# Revit family: CADS_AIRFLOWdev_AirflexPro_Round_DistributionBox_6PortNarrow
name_source: partatom
category: Duct Accessories
units: mm (PartAtom-declared; Revit-internal decimal feet)

## family parameters
Always vertical = Yes
Cut with Voids When Loaded = No
OmniClass Number = 23.75.00.00
OmniClass Title = Climate Control (HVAC)
Part Type = Breaks Into
Round Connector Dimension = Use Diameter
Shared = No
Work Plane-Based = No

## types (1)
- CADS_AIRFLOWdev_AirflexPro_Round_DistributionBox_6PortNarrow
    6MonthlyMaintenance = Visually inspect system, clean the fan and ducting if necessary
    AirflowRateRange = 54.0 L/s
    AssemblyPlace = UNKNOWN
    AssetType = FIXED
    Body = CADS_AIRFLOWdev_SteelGalvanized
    CADS_Index = 0
    CEApproval = Yes
    Color = Silver
    Conn_IDia = 125 mm  [stored 0.410105 ft]
    Constituents = 6-Spigot In-line Distribution Box . Round spigots & sound insulation fitted - Narrow
    DurationUnit = Year
    ExpectedServiceLife = 10
    Features = 6-Spigot In-line Distribution Box . Round spigots & sound insulation fitted - Narrow
    Finish = Lacquer
    FireControlPanelLinks = No
    Fitting Type = Ignore
    Grade = Stainless
    GrossWeight = 5.05 kg
    Halfb1 = 150 mm  [stored 0.492126 ft]
    ISO140001 = Yes
    ISO90001 = Yes
    IsExtendedWarranty = No
    LongitudinalSeam = None
    Manufacturer = Airflow Developments Ltd
    ManufacturerAddress = Aidelle House
Lancaster Road
Cressex Business Park
High Wycombe
Bucks
HP123QP
    ManufacturerTelephone = 01494 525252
    ManufacturerWebsite = www.airflow.com
    Material = Steel
    NBSCode = 45-80-50/394 Ventilation ducts
    NominalHeight = 200 mm  [stored 0.656168 ft]
    NominalLength = 400 mm  [stored 1.31234 ft]
    NominalWidth = 300 mm
    PassiveHouseApproval = No
    PointOfContact = Airflow Developments Ltd
    ProductLiterature = https://www.airflow.com
    ProductionYear = 2017
    Quantity = 1
    RedDotDesignAward = No
    ReplacementCost = 334.62
    SAPApproval = Yes
    ServiceLifeDuration = 10
    ServiceLifeType = EXPECTEDSERVICELIFE
    Shape = Rectangular
    ShippingWeight = 6.06 kg
    Size = 400 x 300 x 200
    Status = New
    TemperatureRange = up to 40°C
    Uniclass2015 = Pr_30_59_96_92:Ventilation ducts
    WarrantyGuarantor = Airflow Developments Ltd
    WarrantyPeriod = 0
    WorkingPressure = 3000.0 Pa
    b1 = 300 mm
    h1 = 200 mm  [stored 0.656168 ft]
    l1 = 400 mm  [stored 1.31234 ft]

note: [stored X ft] marks values corroborated as IEEE doubles in the binary element streams (Revit-internal decimal feet)

## geometry (parser evidence)
native form markers: Blend x6, Sweep x24
no freeform markers — native parametric forms only
